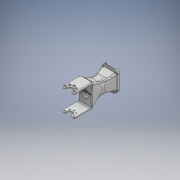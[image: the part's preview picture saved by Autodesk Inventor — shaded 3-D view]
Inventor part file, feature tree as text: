
AUTODESK INVENTOR PART (.ipt)
format: ipt  version: 2019 (Build 230136000, 136)  size: 1,804,800 bytes
history: native  units: mm
features: fillet x16, sketch x15, extrude x12, plane x8, projected_geometry x8, mirror x2, loft x2, other x1
ambient origin geometry x8: Origin, YZ Plane, XZ Plane, XY Plane, X Axis, Y Axis, Z Axis, Center Point
bodies: Solid1 (feature_tree)
feature tree (64):
  extrude  "Extrusion1"  Depth=47.0mm
  sketch  "Sketch2"  dims[d2=4.0mm d3=0.0mm d4=25.0mm]
  plane  "Work Plane1"
  plane  "Work Plane2"
  extrude  "Extrusion3"  Depth=4.0mm
  mirror  "Mirror1"
  plane  "Work Plane6"
  extrude  "Extrusion4"  Depth=22.0mm
  plane  "Work Plane7"
  extrude  "Extrusion5"  Depth=80.0mm TaperAngle=360.0deg
  extrude  "Extrusion6"  TaperAngle=180.0deg  [1 undecoded]
  fillet  "Fillet3"  [1 undecoded]
  plane  "Work Plane4"
  extrude  "Extrusion7"  Depth=4.0mm
  plane  "Work Plane3"
  extrude  "Extrusion8"  Depth=5.0mm TaperAngle=0.0deg
  plane  "Work Plane8"
  extrude  "Extrusion11"  Depth=2.0mm
  extrude  "Extrusion12"  Depth=1.5mm TaperAngle=0.0deg
  mirror  "Mirror2"
  sketch  "3D Sketch2"
  plane  "Work Plane5"
  loft  "Loft1"
  loft  "Loft2"
  fillet  "Fillet10"  Radius=5.2mm
  fillet  "Fillet11"  Radius=5.2mm
  extrude  "Extrusion13"  Depth=2.0mm
  fillet  "Fillet12"  Radius=20.0mm
  fillet  "Fillet13"  Radius=2.0mm
  fillet  "Fillet14"  Radius=26.0mm
  fillet  "Fillet15"  Radius=41.0mm
  fillet  "Fillet16"  Radius=5.2mm
  fillet  "Fillet17"  Radius=5.2mm
  extrude  "Extrusion14"  Depth=5.2mm
  extrude  "Extrusion16"  Depth=2.0mm TaperAngle=0.0deg
  fillet  "Fillet18"  Radius=15.0mm
  fillet  "Fillet19"  Radius=30.25mm
  fillet  "Fillet20"  [1 undecoded]
  fillet  "Fillet21"  [1 undecoded]
  fillet  "Fillet22"  [1 undecoded]
  fillet  "Fillet23"  [1 undecoded]
  fillet  "Fillet24"  Radius=16.0mm
  sketch  "Sketch1"  dims[d0=30.0mm d1=47.0mm]
  sketch  "Sketch3"  dims[d8=36.0mm d9=22.0mm]
  projected_geometry  "Projected Loop1"
  sketch  "Sketch4"  dims[d10=2.8mm d11=80.0mm d13=360.0deg]
  sketch  "Sketch6"  dims[d15=7.0mm d16=180.0deg d17=180.0deg]
  sketch  "Sketch7"  dims[d18=4.0mm d19=0.0mm d25=20.0mm d27=30.0mm d28=20.0mm d30=17.0mm]
  projected_geometry  "Projected Loop4"
  projected_geometry  "Projected Loop7"
  projected_geometry  "Projected Loop8"
  sketch  "Sketch12"  dims[d33=6.0mm d34=0.0mm d36=5.0mm d37=0.0mm]
  sketch  "Sketch13"  dims[d40=2.0mm d41=0.0mm d47=2.0mm]
  projected_geometry  "Projected Loop11"
  sketch  "Sketch15"  dims[d52=20.0mm d53=0.0mm d59=1.5mm d60=0.0mm]
  sketch  "Sketch16"  dims[d73=5.2mm d74=5.2mm]
  sketch  "Sketch17"  dims[d75=5.2mm d76=5.2mm d77=5.2mm d78=5.2mm]
  other  "Edges1"
  sketch  "Sketch18"  dims[d79=5.2mm d80=5.2mm d81=20.0mm d82=2.0mm d83=0.0mm d85=26.0mm d86=41.0mm d88=5.2mm d89=5.2mm]
  sketch  "Sketch19"  dims[d90=5.2mm d91=5.2mm]
  projected_geometry  "Projected Loop12"
  sketch  "Sketch20"  dims[d92=5.2mm d93=2.0mm d94=0.0mm d95=15.0mm d96=0.0mm d97=30.25mm d98=0.0mm d99=90.0deg d100=0.0mm d101=90.0deg d102=0.0mm d103=90.0deg d104=0.0mm d105=90.0deg d106=16.0mm d107=5.0mm d108=10.0mm d109=0.0mm d110=2.0mm d111=16.0mm d112=16.0mm d113=4.0mm d114=4.0mm d115=30.0mm d116=15.0mm d117=0.0mm d118=5.2mm d121=15.0mm d122=0.0mm d123=1.0mm d124=0.5mm d125=0.5mm d126=0.5mm d127=8.0mm d128=8.0mm d129=2.0mm]
  projected_geometry  "Projected Loop13"
  projected_geometry  "Projected Loop14"
note: 6 required parameter values undecoded (feature->parameter linkage not recoverable at this tier; creation-order binding heuristic only, values carry confidence <= 0.55)
